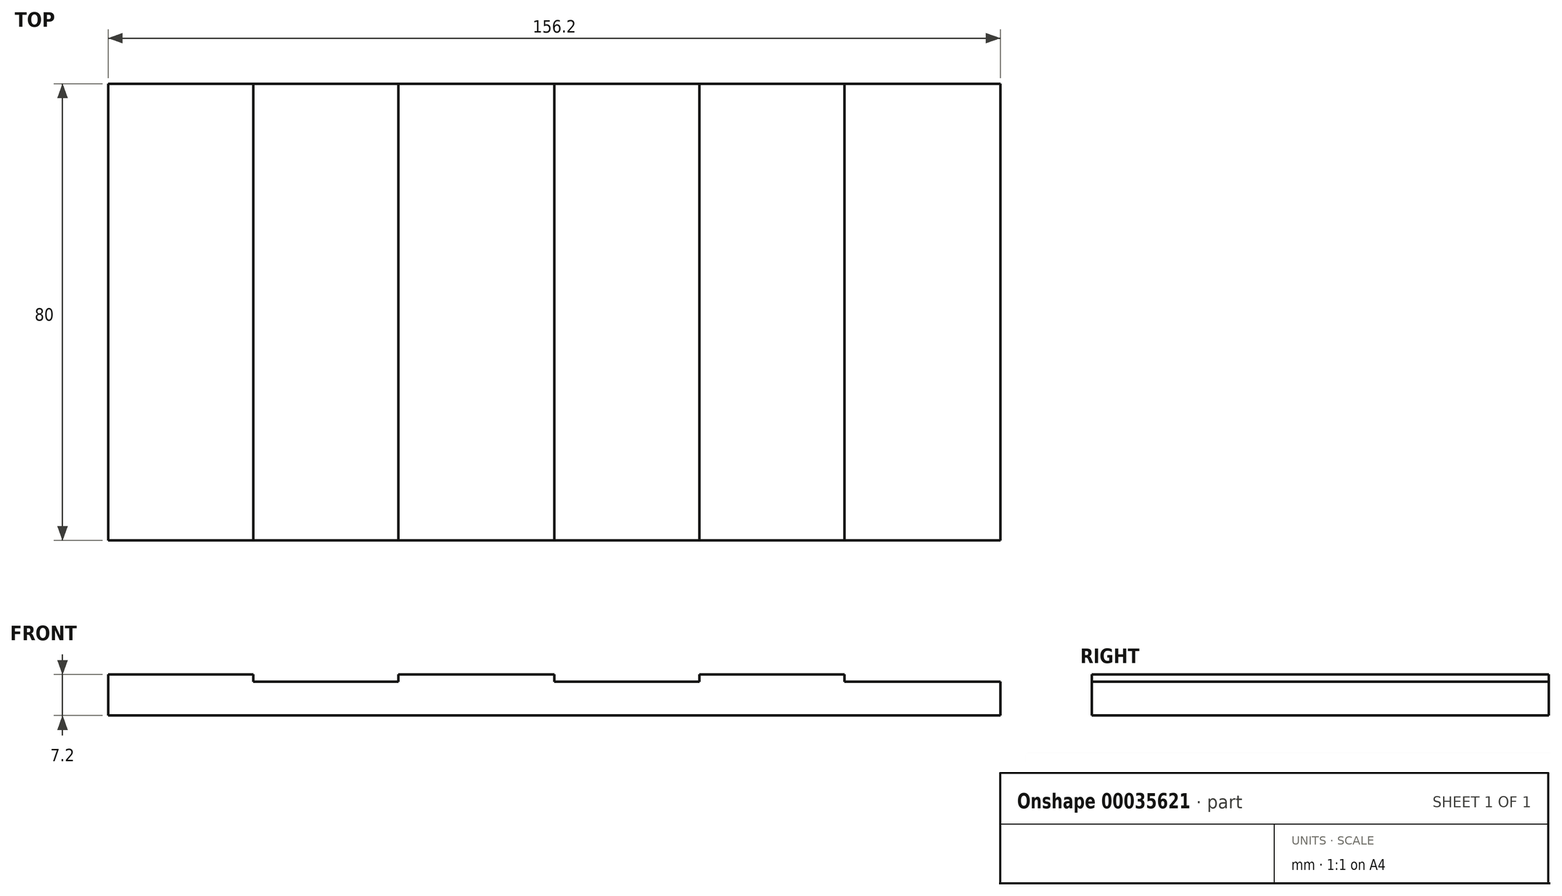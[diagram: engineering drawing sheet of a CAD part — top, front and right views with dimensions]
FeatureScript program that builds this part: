
annotation { "Feature Type Name" : "Feature", "Feature Type Description" : "" }
export const myFeature = defineFeature(function(context is Context, id is Id, definition is map)
    precondition{}
    {
        {
            var Q0;
            Q0=qCreatedBy(makeId("Top.planeOp"),FACE);
            var sketch = newSketch(context, id + "F0", { "sketchPlane" : qUnion([Q0])});
            skLineSegment(sketch, "E0.rect.bottom", {"start": v(78.1, 40) * mm, "end": v(-78.1, 40) * mm});
            skLineSegment(sketch, "E0.rect.top", {"start": v(78.1, -40) * mm, "end": v(-78.1, -40) * mm});
            skLineSegment(sketch, "E0.rect.left", {"start": v(78.1, 40) * mm, "end": v(78.1, -40) * mm});
            skLineSegment(sketch, "E0.rect.right", {"start": v(-78.1, 40) * mm, "end": v(-78.1, -40) * mm});
            skPoint(sketch, "E0.rect.middle", {"position": v(0, 0) * mm});
            skSolve(sketch);
        }
        {
            var Q0;
            Q0 = qSketchRegion(id + "F0", true);
            extrude(context, id + "F1", {"entities" : qUnion([Q0]), "depth" : 8.47 * mm});
        }
        {
            var Q0;
            Q0=makeQuery(id+"F1.opExtrude","CAP_FACE",FACE,{"disambiguationData":[OSD([sQuery(id+"F0.wireOp",EDGE,"E0.rect.bottom"),sQuery(id+"F0.wireOp",EDGE,"E0.rect.top"),sQuery(id+"F0.wireOp",EDGE,"E0.rect.left"),sQuery(id+"F0.wireOp",EDGE,"E0.rect.right")])],"isStart":false});
            var sketch = newSketch(context, id + "F2", { "sketchPlane" : qUnion([Q0])});
            skLineSegment(sketch, "E1.bottom", {"start": v(-78.1, 40) * mm, "end": v(-52.7, 40) * mm});
            skLineSegment(sketch, "E1.top", {"start": v(-78.1, -40) * mm, "end": v(-52.7, -40) * mm});
            skLineSegment(sketch, "E1.left", {"start": v(-78.1, 40) * mm, "end": v(-78.1, -40) * mm});
            skLineSegment(sketch, "E1.right", {"start": v(-52.7, 40) * mm, "end": v(-52.7, -40) * mm});
            skLineSegment(sketch, "E2.bottom", {"start": v(-52.7, 40) * mm, "end": v(-27.3, 40) * mm});
            skLineSegment(sketch, "E2.top", {"start": v(-52.7, -40) * mm, "end": v(-27.3, -40) * mm});
            skLineSegment(sketch, "E2.right", {"start": v(-27.3, 40) * mm, "end": v(-27.3, -40) * mm});
            skLineSegment(sketch, "E3.bottom", {"start": v(-27.3, 40) * mm, "end": v(0, 40) * mm});
            skLineSegment(sketch, "E3.top", {"start": v(-27.3, -40) * mm, "end": v(0, -40) * mm});
            skLineSegment(sketch, "E3.right", {"start": v(0, 40) * mm, "end": v(0, -40) * mm});
            skLineSegment(sketch, "E4.bottom", {"start": v(0, 40) * mm, "end": v(25.4, 40) * mm});
            skLineSegment(sketch, "E4.top", {"start": v(0, -40) * mm, "end": v(25.4, -40) * mm});
            skLineSegment(sketch, "E4.right", {"start": v(25.4, 40) * mm, "end": v(25.4, -40) * mm});
            skLineSegment(sketch, "E5.bottom", {"start": v(25.4, 40) * mm, "end": v(50.8, 40) * mm});
            skLineSegment(sketch, "E5.top", {"start": v(25.4, -40) * mm, "end": v(50.8, -40) * mm});
            skLineSegment(sketch, "E5.right", {"start": v(50.8, 40) * mm, "end": v(50.8, -40) * mm});
            skLineSegment(sketch, "E6.bottom", {"start": v(50.8, 40) * mm, "end": v(78.1, 40) * mm});
            skLineSegment(sketch, "E6.top", {"start": v(50.8, -40) * mm, "end": v(78.1, -40) * mm});
            skLineSegment(sketch, "E6.right", {"start": v(78.1, 40) * mm, "end": v(78.1, -40) * mm});
            skSolve(sketch);
        }
        {
            var Q0;
            Q0=makeQuery(id+"F2.imprint","IMPRINT",FACE,{"disambiguationData":[TD([[makeQuery(id+"F2.imprint","IMPRINT",EDGE,{"derivedFrom":sQuery(id+"F2.wireOp",EDGE,"E1.bottom")}),1.0]])]});
            extrude(context, id + "F3", {"entities" : qUnion([Q0]), "operationType" : NewBodyOperationType.REMOVE, "oppositeDirection" : true, "depth" : 1.27 * mm});
        }
        {
            var Q0;
            Q0=makeQuery(id+"F2.imprint","IMPRINT",FACE,{"disambiguationData":[TD([[makeQuery(id+"F2.imprint","IMPRINT",EDGE,{"derivedFrom":sQuery(id+"F2.wireOp",EDGE,"E2.bottom")}),1.0]])]});
            extrude(context, id + "F4", {"entities" : qUnion([Q0]), "operationType" : NewBodyOperationType.REMOVE, "oppositeDirection" : true, "depth" : 2.54 * mm});
        }
        {
            var Q0;
            Q0=makeQuery(id+"F2.imprint","IMPRINT",FACE,{"disambiguationData":[TD([[makeQuery(id+"F2.imprint","IMPRINT",EDGE,{"derivedFrom":sQuery(id+"F2.wireOp",EDGE,"E3.bottom")}),1.0]])]});
            extrude(context, id + "F5", {"entities" : qUnion([Q0]), "operationType" : NewBodyOperationType.REMOVE, "oppositeDirection" : true, "depth" : 1.27 * mm});
        }
        {
            var Q0;
            Q0=makeQuery(id+"F2.imprint","IMPRINT",FACE,{"disambiguationData":[TD([[makeQuery(id+"F2.imprint","IMPRINT",EDGE,{"derivedFrom":sQuery(id+"F2.wireOp",EDGE,"E4.bottom")}),1.0]])]});
            extrude(context, id + "F6", {"entities" : qUnion([Q0]), "operationType" : NewBodyOperationType.REMOVE, "oppositeDirection" : true, "depth" : 2.54 * mm});
        }
        {
            var Q0;
            Q0=makeQuery(id+"F2.imprint","IMPRINT",FACE,{"disambiguationData":[TD([[makeQuery(id+"F2.imprint","IMPRINT",EDGE,{"derivedFrom":sQuery(id+"F2.wireOp",EDGE,"E5.bottom")}),1.0]])]});
            extrude(context, id + "F7", {"entities" : qUnion([Q0]), "operationType" : NewBodyOperationType.REMOVE, "oppositeDirection" : true, "depth" : 1.27 * mm});
        }
        {
            var Q0;
            Q0=makeQuery(id+"F2.imprint","IMPRINT",FACE,{"disambiguationData":[TD([[makeQuery(id+"F2.imprint","IMPRINT",EDGE,{"derivedFrom":sQuery(id+"F2.wireOp",EDGE,"E6.bottom")}),1.0]])]});
            extrude(context, id + "F8", {"entities" : qUnion([Q0]), "operationType" : NewBodyOperationType.REMOVE, "oppositeDirection" : true, "depth" : 2.54 * mm});
        }
    });
